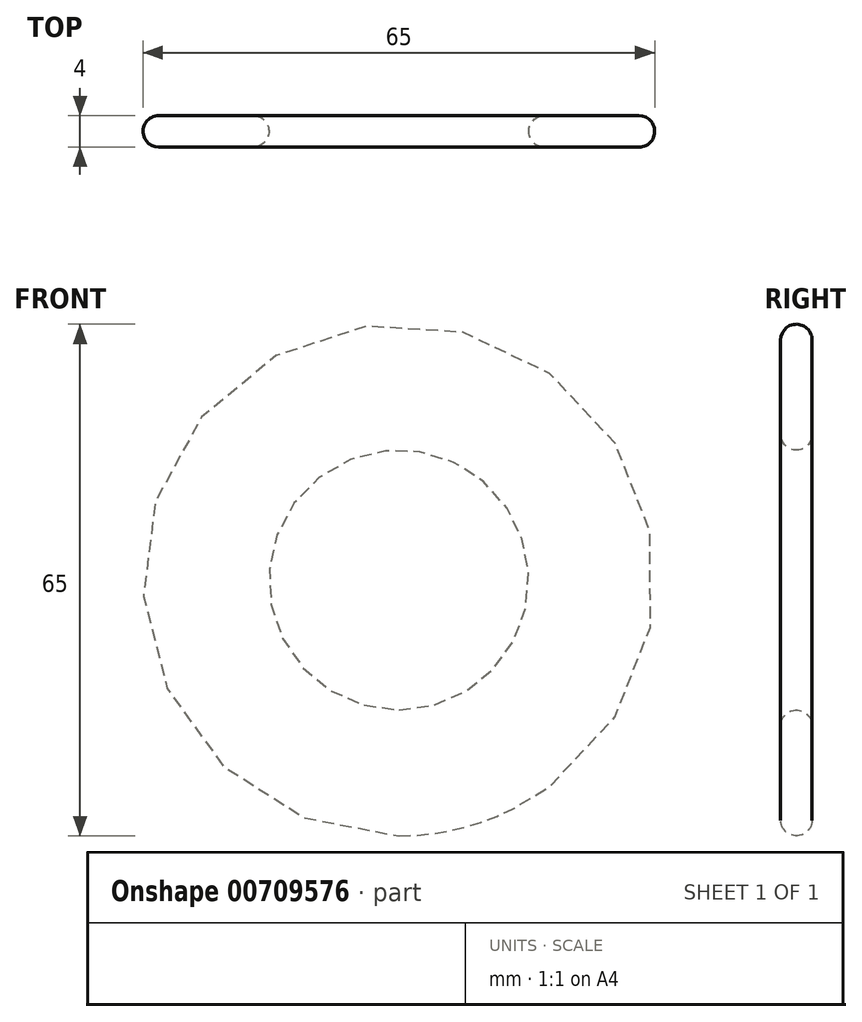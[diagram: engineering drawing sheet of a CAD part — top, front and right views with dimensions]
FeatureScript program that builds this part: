
annotation { "Feature Type Name" : "Feature", "Feature Type Description" : "" }
export const myFeature = defineFeature(function(context is Context, id is Id, definition is map)
    precondition{}
    {
        {
            var Q0;
            Q0=qCreatedBy(makeId("Front.planeOp"),FACE);
            var sketch = newSketch(context, id + "F0", { "sketchPlane" : qUnion([Q0])});
            skCircle(sketch, "E0", {"center": v(0, 0) * mm, "radius": 16.5 * mm});
            skCircle(sketch, "E1", {"center": v(0, 0) * mm, "radius": 32.5 * mm});
            skPoint(sketch, "E2.start.orphan", {"position": v(-32.5, 0) * mm});
            skPoint(sketch, "E3.start.orphan", {"position": v(-16.5, 0) * mm});
            skPoint(sketch, "E4.orphan", {"position": v(16.5, 0) * mm});
            skPoint(sketch, "E5.start.orphan", {"position": v(32.5, 0) * mm});
            skPoint(sketch, "E6.center.orphan", {"position": v(0, 34.3) * mm});
            skPoint(sketch, "E7.center.orphan", {"position": v(34.3, 0) * mm});
            skPoint(sketch, "E8.center.orphan", {"position": v(0, -34.3) * mm});
            skPoint(sketch, "E9.center.orphan", {"position": v(-34.3, 0) * mm});
            skSolve(sketch);
        }
        {
            var Q0;
            {var subQ0=sQuery(id+"F0.wireOp",EDGE,"E3");var subQ1=sQuery(id+"F0.wireOp",EDGE,"E0");var subQ2=makeQuery(id+"F0.imprint","INTERSECT",VERTEX,{"derivedFrom":[subQ1,subQ0]});Q0=makeQuery(id+"F0.imprint","IMPRINT",FACE,{"disambiguationData":[TD([[makeQuery(id+"F0.imprint","IMPRINT",EDGE,{"disambiguationData":[TD([[subQ2,1.0]])],"derivedFrom":subQ1}),-1.0]])]});}
            var Q1;
            {var subQ3=sQuery(id+"F0.wireOp",EDGE,"E3");var subQ7=sQuery(id+"F0.wireOp",EDGE,"E0");var subQ8=makeQuery(id+"F0.imprint","INTERSECT",VERTEX,{"derivedFrom":[subQ7,subQ3]});Q1=makeQuery(id+"F0.imprint","IMPRINT",FACE,{"disambiguationData":[TD([[makeQuery(id+"F0.imprint","IMPRINT",EDGE,{"disambiguationData":[TD([[subQ8,-1.0]])],"derivedFrom":subQ7}),-1.0]])]});}
            var Q2;
            Q2=makeQuery(id+"F0.imprint","IMPRINT",FACE,{"disambiguationData":[TD([[makeQuery(id+"F0.imprint","IMPRINT",EDGE,{"derivedFrom":sQuery(id+"F0.wireOp",EDGE,"E0")}),-1.0]])]});
            extrude(context, id + "F1", {"entities" : qUnion([Q0, Q1, Q2]), "depth" : 4 * mm, "offsetDistance" : 25.4 * mm});
        }
        {
            var Q0;
            Q0=makeQuery(id+"F1.opExtrude","CAP_EDGE",EDGE,{"disambiguationData":[OSD([sQuery(id+"F0.wireOp",EDGE,"E1")])],"isStart":false});
            var Q1;
            Q1=makeQuery(id+"F1.opExtrude","CAP_EDGE",EDGE,{"disambiguationData":[OSD([sQuery(id+"F0.wireOp",EDGE,"E1")])],"isStart":true});
            var Q2;
            Q2=makeQuery(id+"F1.opExtrude","CAP_EDGE",EDGE,{"disambiguationData":[OSD([sQuery(id+"F0.wireOp",EDGE,"E0")])],"isStart":true});
            var Q3;
            Q3=makeQuery(id+"F1.opExtrude","CAP_EDGE",EDGE,{"disambiguationData":[OSD([sQuery(id+"F0.wireOp",EDGE,"E0")])],"isStart":false});
            fillet(context, id + "F2", {"entities" : qUnion([Q0, Q1, Q2, Q3]), "radius" : 2 * mm, "tangentPropagation" : true, "allowEdgeOverflow" : false});
        }
    });
